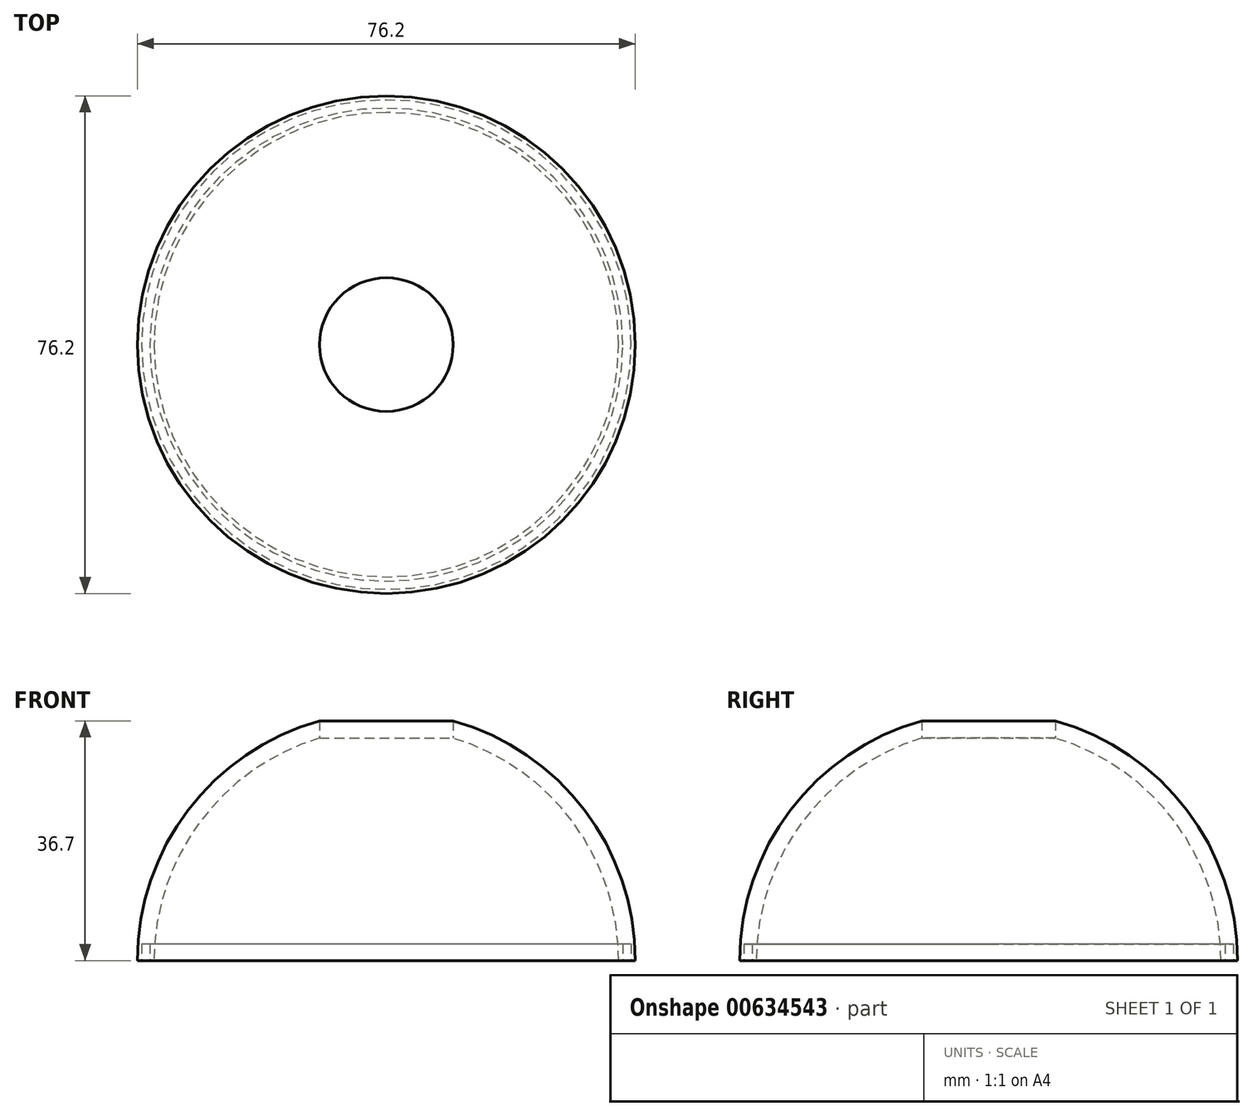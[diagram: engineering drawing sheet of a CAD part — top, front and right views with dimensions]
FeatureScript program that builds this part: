
annotation { "Feature Type Name" : "Feature", "Feature Type Description" : "" }
export const myFeature = defineFeature(function(context is Context, id is Id, definition is map)
    precondition{}
    {
        {
            var Q0;
            Q0=qCreatedBy(makeId("Top.planeOp"),FACE);
            var sketch = newSketch(context, id + "F0", { "sketchPlane" : qUnion([Q0])});
            skArc(sketch, "E0", {"start": v(38.1, 0) * mm, "mid": v(0, 38.1) * mm, "end": v(-38.1, 0) * mm});
            skLineSegment(sketch, "E1", {"start": v(-38.1, 0) * mm, "end": v(38.1, 0) * mm});
            skSolve(sketch);
        }
        {
            var Q0;
            Q0 = qSketchRegion(id + "F0", true);
            var Q1;
            Q1=sQuery(id+"F0.wireOp",EDGE,"E1");
            revolve(context, id + "F1", {"entities" : qUnion([Q0]), "axis" : qUnion([Q1]), "revolveType" : RevolveType.ONE_DIRECTION, "angle" : 180 * degree});
        }
        {
            var Q0;
            Q0=makeQuery(id+"F1.opRevolve","CAP_FACE",FACE,{"disambiguationData":[OSD([sQuery(id+"F0.wireOp",EDGE,"E0"),sQuery(id+"F0.wireOp",EDGE,"E1")])],"isStart":true});
            shell(context, id + "F2", {"entities" : qUnion([Q0]), "thickness" : 2.54 * mm});
        }
        {
            var Q0;
            Q0=qCreatedBy(makeId("Top.planeOp"),FACE);
            var sketch = newSketch(context, id + "F3", { "sketchPlane" : qUnion([Q0])});
            skCircle(sketch, "E2.0", {"center": v(0, 0) * mm, "radius": 36.2 * mm});
            skCircle(sketch, "E3.0", {"center": v(0, 0) * mm, "radius": 37.47 * mm});
            skSolve(sketch);
        }
        {
            var Q0;
            Q0 = qSketchRegion(id + "F3", true);
            extrude(context, id + "F4", {"entities" : qUnion([Q0]), "operationType" : NewBodyOperationType.REMOVE, "depth" : 2.54 * mm, "offsetDistance" : 25.4 * mm});
        }
        {
            var Q0;
            Q0=qCreatedBy(makeId("Top.planeOp"),FACE);
            var sketch = newSketch(context, id + "F5", { "sketchPlane" : qUnion([Q0])});
            skCircle(sketch, "E4", {"center": v(0, 0) * mm, "radius": 10.24 * mm});
            skSolve(sketch);
        }
        {
            var Q0;
            Q0 = qSketchRegion(id + "F5", true);
            extrude(context, id + "F6", {"entities" : qUnion([Q0]), "operationType" : NewBodyOperationType.REMOVE, "depth" : 101.6 * mm, "offsetDistance" : 25.4 * mm});
        }
    });
